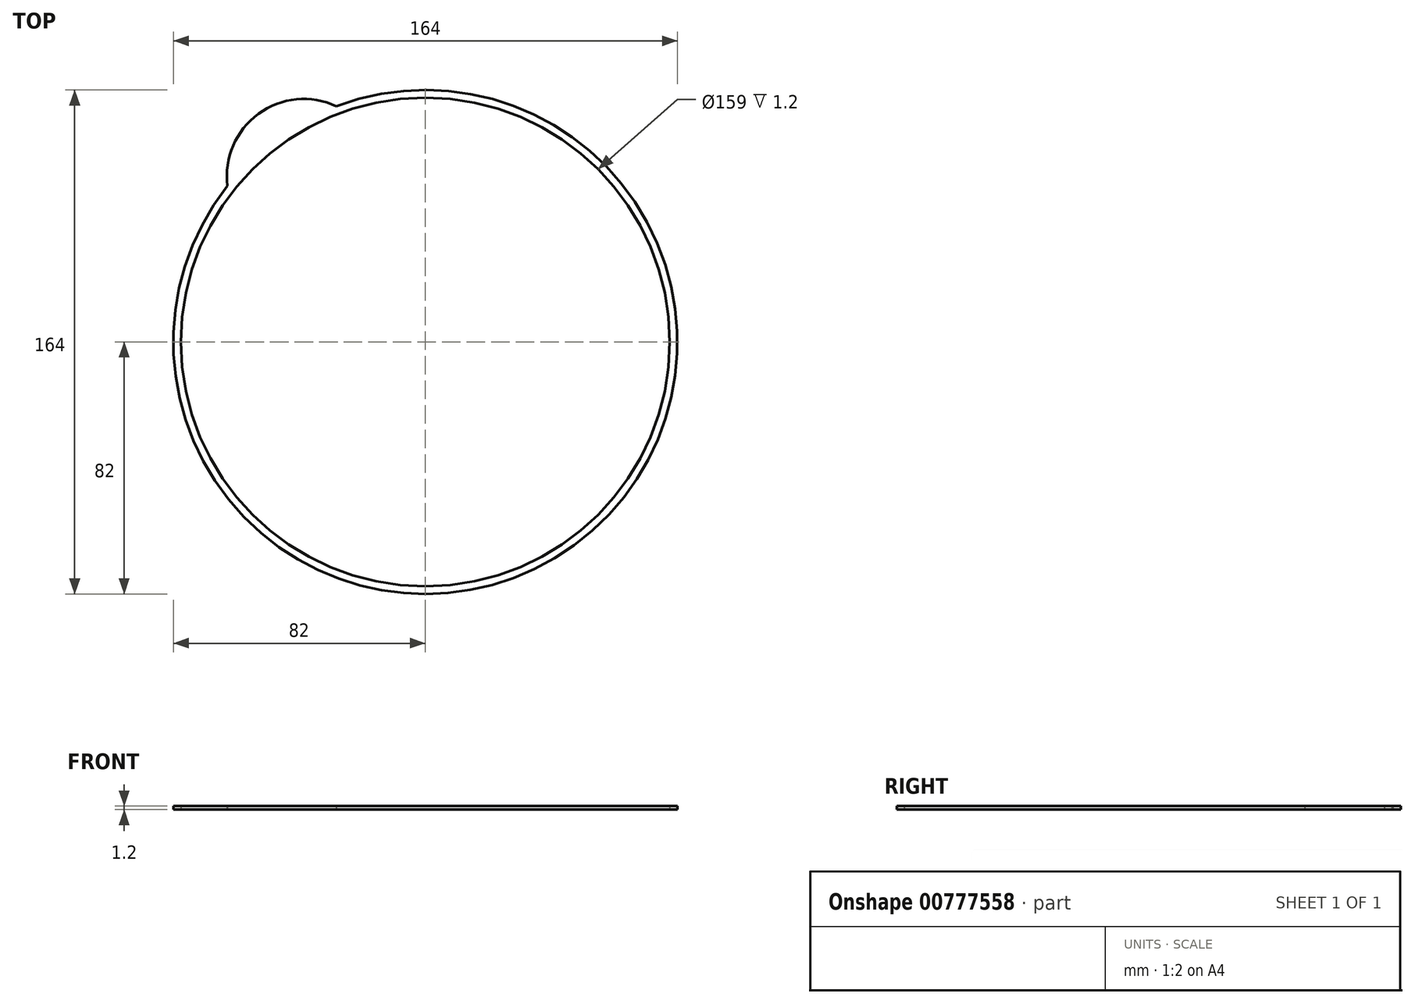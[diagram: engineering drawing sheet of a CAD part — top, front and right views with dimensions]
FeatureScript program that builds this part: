
annotation { "Feature Type Name" : "Feature", "Feature Type Description" : "" }
export const myFeature = defineFeature(function(context is Context, id is Id, definition is map)
    precondition{}
    {
        {
            var Q0;
            Q0=qCreatedBy(makeId("Top.planeOp"),FACE);
            var sketch = newSketch(context, id + "F0", { "sketchPlane" : qUnion([Q0])});
            skCircle(sketch, "E0", {"center": v(0, 0) * mm, "radius": 79.5 * mm});
            skCircle(sketch, "E1", {"center": v(0, 0) * mm, "radius": 82 * mm});
            skArc(sketch, "E2", {"start": v(-28.93, 76.73) * mm, "mid": v(-54.3, 74.25) * mm, "end": v(-64.36, 50.8) * mm});
            skLineSegment(sketch, "E3", {"start": v(0, 0) * mm, "end": v(56.37, 56.06) * mm});
            skArc(sketch, "E4.MirrorCS", {"start": v(76.57, -29.34) * mm, "mid": v(73.95, -54.7) * mm, "end": v(50.46, -64.64) * mm});
            skSolve(sketch);
        }
        {
            var Q0;
            Q0=makeQuery(id+"F0.imprint","IMPRINT",FACE,{"disambiguationData":[TD([[makeQuery(id+"F0.imprint","IMPRINT",EDGE,{"derivedFrom":sQuery(id+"F0.wireOp",EDGE,"E0")}),-1.0]])]});
            var Q1;
            {var subQ0=sQuery(id+"F0.wireOp",EDGE,"E2");Q1=makeQuery(id+"F0.imprint","IMPRINT",FACE,{"disambiguationData":[TD([[makeQuery(id+"F0.imprint","IMPRINT",EDGE,{"derivedFrom":subQ0}),1.0]])]});}
            var Q2;
            {var subQ0=sQuery(id+"F0.wireOp",EDGE,"E4.MirrorCS");Q2=makeQuery(id+"F0.imprint","IMPRINT",FACE,{"disambiguationData":[TD([[makeQuery(id+"F0.imprint","IMPRINT",EDGE,{"derivedFrom":subQ0}),-1.0]])]});}
            extrude(context, id + "F1", {"entities" : qUnion([Q0, Q1, Q2]), "depth" : 1.2 * mm, "offsetDistance" : 25 * mm});
        }
    });
